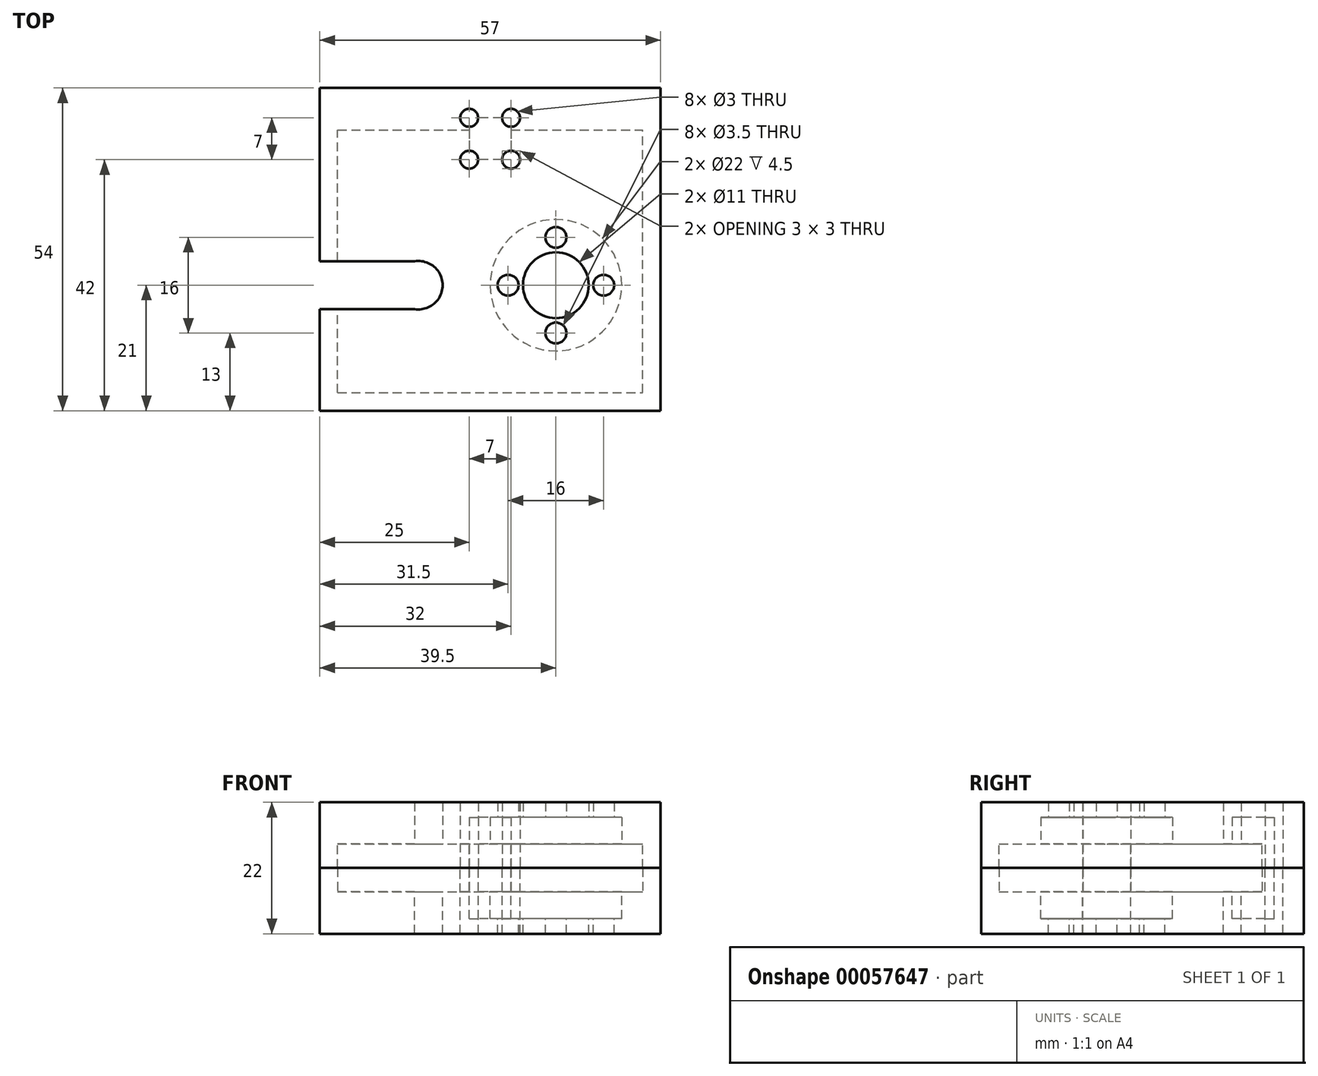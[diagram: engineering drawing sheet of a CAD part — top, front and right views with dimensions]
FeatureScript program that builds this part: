
annotation { "Feature Type Name" : "Feature", "Feature Type Description" : "" }
export const myFeature = defineFeature(function(context is Context, id is Id, definition is map)
    precondition{}
    {
        {
            var Q0;
            Q0=qCreatedBy(makeId("Top.planeOp"),FACE);
            var sketch = newSketch(context, id + "F0", { "sketchPlane" : qUnion([Q0])});
            skCircle(sketch, "E0", {"center": v(0, 0) * mm, "radius": 5.5 * mm});
            skCircle(sketch, "E1", {"center": v(0, 0) * mm, "radius": 8 * mm, "construction": true});
            skCircle(sketch, "E2", {"center": v(0, 8) * mm, "radius": 1.75 * mm});
            skCircle(sketch, "E3", {"center": v(8, 0) * mm, "radius": 1.75 * mm});
            skCircle(sketch, "E4", {"center": v(0, -8) * mm, "radius": 1.75 * mm});
            skCircle(sketch, "E5", {"center": v(-8, 0) * mm, "radius": 1.75 * mm});
            skCircle(sketch, "E6", {"center": v(0, 0) * mm, "radius": 11 * mm});
            skLineSegment(sketch, "E7.rect.bottom", {"start": v(-7.5, 28) * mm, "end": v(-14.5, 28) * mm});
            skLineSegment(sketch, "E7.rect.top", {"start": v(-7.5, 21) * mm, "end": v(-14.5, 21) * mm});
            skLineSegment(sketch, "E7.rect.left", {"start": v(-7.5, 28) * mm, "end": v(-7.5, 21) * mm});
            skLineSegment(sketch, "E7.rect.right", {"start": v(-14.5, 28) * mm, "end": v(-14.5, 21) * mm});
            skLineSegment(sketch, "E8.rect.bottom", {"start": v(14.5, -21) * mm, "end": v(-36.5, -21) * mm});
            skLineSegment(sketch, "E8.rect.top", {"start": v(14.5, 33) * mm, "end": v(-36.5, 33) * mm});
            skLineSegment(sketch, "E8.rect.left", {"start": v(14.5, -21) * mm, "end": v(14.5, 33) * mm});
            skLineSegment(sketch, "E8.rect.right", {"start": v(-36.5, -21) * mm, "end": v(-36.5, 33) * mm});
            skPoint(sketch, "E8.rect.middle", {"position": v(-11, 6) * mm});
            skLineSegment(sketch, "E9", {"start": v(-36.5, 26) * mm, "end": v(-14.5, 26) * mm});
            skLineSegment(sketch, "E10", {"start": v(-36.5, -18) * mm, "end": v(14.5, -18) * mm});
            skCircle(sketch, "E11", {"center": v(-14.5, 28) * mm, "radius": 1.5 * mm});
            skCircle(sketch, "E12", {"center": v(-7.5, 28) * mm, "radius": 1.5 * mm});
            skCircle(sketch, "E13", {"center": v(-7.5, 21) * mm, "radius": 1.5 * mm});
            skCircle(sketch, "E14", {"center": v(-14.5, 21) * mm, "radius": 1.5 * mm});
            skCircle(sketch, "E15", {"center": v(-23, 0) * mm, "radius": 4.05 * mm});
            skLineSegment(sketch, "E16.bottom", {"start": v(-39.5, 33) * mm, "end": v(17.5, 33) * mm});
            skLineSegment(sketch, "E16.top", {"start": v(-39.5, -21) * mm, "end": v(17.5, -21) * mm});
            skLineSegment(sketch, "E16.left", {"start": v(-39.5, 33) * mm, "end": v(-39.5, -21) * mm});
            skLineSegment(sketch, "E16.right", {"start": v(17.5, 33) * mm, "end": v(17.5, -21) * mm});
            skPoint(sketch, "E17.endSnap0", {"position": v(-11, 21) * mm});
            skLineSegment(sketch, "E18", {"start": v(-11, 21) * mm, "end": v(-11, 28) * mm, "construction": true});
            skLineSegment(sketch, "E19", {"start": v(-11, 26) * mm, "end": v(-11, 33) * mm, "construction": true});
            skLineSegment(sketch, "E20", {"start": v(-11, 26) * mm, "end": v(-11, 24.5) * mm, "construction": true});
            skLineSegment(sketch, "E21.trimOffspring", {"start": v(-7.5, 26) * mm, "end": v(14.5, 26) * mm});
            skLineSegment(sketch, "E22", {"start": v(-23, 0) * mm, "end": v(-39.5, 0) * mm, "construction": true});
            skLineSegment(sketch, "E23.0", {"start": v(-23, 4) * mm, "end": v(-39.5, 4) * mm});
            skLineSegment(sketch, "E24.0", {"start": v(-23, -4) * mm, "end": v(-39.5, -4) * mm});
            skSolve(sketch);
        }
        {
            var Q0;
            Q0=makeQuery(id+"F0.imprint","IMPRINT",FACE,{"disambiguationData":[TD([[makeQuery(id+"F0.imprint","IMPRINT",EDGE,{"derivedFrom":sQuery(id+"F0.wireOp",EDGE,"E6")}),-1.0]])]});
            var Q1;
            {var subQ0=sQuery(id+"F0.wireOp",EDGE,"E9");Q1=makeQuery(id+"F0.imprint","IMPRINT",FACE,{"disambiguationData":[TD([[makeQuery(id+"F0.imprint","IMPRINT",EDGE,{"derivedFrom":subQ0}),1.0]])]});}
            var Q2;
            {var subQ3=sQuery(id+"F0.wireOp",EDGE,"E10");Q2=makeQuery(id+"F0.imprint","IMPRINT",FACE,{"disambiguationData":[TD([[makeQuery(id+"F0.imprint","IMPRINT",EDGE,{"derivedFrom":subQ3}),-1.0]])]});}
            var Q3;
            {var subQ3=sQuery(id+"F0.wireOp",EDGE,"E16.right");Q3=makeQuery(id+"F0.imprint","IMPRINT",FACE,{"disambiguationData":[TD([[makeQuery(id+"F0.imprint","IMPRINT",EDGE,{"derivedFrom":subQ3}),-1.0]])]});}
            var Q4;
            {var subQ5=sQuery(id+"F0.wireOp",EDGE,"E8.rect.right");var subQ8=makeQuery(id+"F0.imprint","INTERSECT",VERTEX,{"derivedFrom":[subQ5,sQuery(id+"F0.wireOp",EDGE,"E9")]});Q4=makeQuery(id+"F0.imprint","IMPRINT",FACE,{"disambiguationData":[TD([[makeQuery(id+"F0.imprint","IMPRINT",EDGE,{"disambiguationData":[TD([[subQ8,1.0]])],"derivedFrom":subQ5}),1.0]])]});}
            var Q5;
            {var subQ0=sQuery(id+"F0.wireOp",EDGE,"E16.top");var subQ1=sQuery(id+"F0.wireOp",EDGE,"E8.rect.right");var subQ2=makeQuery(id+"F0.imprint","INTERSECT",VERTEX,{"derivedFrom":[subQ1,subQ0]});Q5=makeQuery(id+"F0.imprint","IMPRINT",FACE,{"disambiguationData":[TD([[makeQuery(id+"F0.imprint","IMPRINT",EDGE,{"disambiguationData":[TD([[subQ2,-1.0]])],"derivedFrom":subQ1}),1.0]])]});}
            extrude(context, id + "F1", {"entities" : qUnion([Q0, Q1, Q2, Q3, Q4, Q5]), "depth" : 4.5 * mm});
        }
        {
            var Q0;
            {var subQ3=sQuery(id+"F0.wireOp",EDGE,"E16.right");Q0=makeQuery(id+"F0.imprint","IMPRINT",FACE,{"disambiguationData":[TD([[makeQuery(id+"F0.imprint","IMPRINT",EDGE,{"derivedFrom":subQ3}),-1.0]])]});}
            var Q1;
            {var subQ0=sQuery(id+"F0.wireOp",EDGE,"E9");Q1=makeQuery(id+"F0.imprint","IMPRINT",FACE,{"disambiguationData":[TD([[makeQuery(id+"F0.imprint","IMPRINT",EDGE,{"derivedFrom":subQ0}),1.0]])]});}
            var Q2;
            {var subQ3=sQuery(id+"F0.wireOp",EDGE,"E10");Q2=makeQuery(id+"F0.imprint","IMPRINT",FACE,{"disambiguationData":[TD([[makeQuery(id+"F0.imprint","IMPRINT",EDGE,{"derivedFrom":subQ3}),-1.0]])]});}
            var Q3;
            {var subQ5=sQuery(id+"F0.wireOp",EDGE,"E8.rect.right");var subQ8=makeQuery(id+"F0.imprint","INTERSECT",VERTEX,{"derivedFrom":[subQ5,sQuery(id+"F0.wireOp",EDGE,"E9")]});Q3=makeQuery(id+"F0.imprint","IMPRINT",FACE,{"disambiguationData":[TD([[makeQuery(id+"F0.imprint","IMPRINT",EDGE,{"disambiguationData":[TD([[subQ8,1.0]])],"derivedFrom":subQ5}),1.0]])]});}
            var Q4;
            {var subQ0=sQuery(id+"F0.wireOp",EDGE,"E16.top");var subQ1=sQuery(id+"F0.wireOp",EDGE,"E8.rect.right");var subQ2=makeQuery(id+"F0.imprint","INTERSECT",VERTEX,{"derivedFrom":[subQ1,subQ0]});Q4=makeQuery(id+"F0.imprint","IMPRINT",FACE,{"disambiguationData":[TD([[makeQuery(id+"F0.imprint","IMPRINT",EDGE,{"disambiguationData":[TD([[subQ2,-1.0]])],"derivedFrom":subQ1}),1.0]])]});}
            extrude(context, id + "F2", {"entities" : qUnion([Q0, Q1, Q2, Q3, Q4]), "operationType" : NewBodyOperationType.ADD, "oppositeDirection" : true, "depth" : 4 * mm});
        }
        {
            var Q0;
            Q0=makeQuery(id+"F1.opExtrude","CAP_FACE",FACE,{"disambiguationData":[OSD([sQuery(id+"F0.wireOp",EDGE,"E6"),sQuery(id+"F0.wireOp",EDGE,"E7.rect.bottom"),sQuery(id+"F0.wireOp",EDGE,"E7.rect.top"),sQuery(id+"F0.wireOp",EDGE,"E7.rect.left"),sQuery(id+"F0.wireOp",EDGE,"E7.rect.right"),sQuery(id+"F0.wireOp",EDGE,"E11"),sQuery(id+"F0.wireOp",EDGE,"E12"),sQuery(id+"F0.wireOp",EDGE,"E13"),sQuery(id+"F0.wireOp",EDGE,"E14"),sQuery(id+"F0.wireOp",EDGE,"E15"),sQuery(id+"F0.wireOp",EDGE,"E16.bottom"),sQuery(id+"F0.wireOp",EDGE,"E16.top"),sQuery(id+"F0.wireOp",EDGE,"E16.left"),sQuery(id+"F0.wireOp",EDGE,"E16.right"),sQuery(id+"F0.wireOp",EDGE,"E23.0"),sQuery(id+"F0.wireOp",EDGE,"E24.0")])],"isStart":false});
            var sketch = newSketch(context, id + "F3", { "sketchPlane" : qUnion([Q0])});
            skLineSegment(sketch, "E25.0", {"start": v(-39.5, -21) * mm, "end": v(17.5, -21) * mm});
            skLineSegment(sketch, "E26.0", {"start": v(17.5, 33) * mm, "end": v(17.5, -21) * mm});
            skLineSegment(sketch, "E27.0", {"start": v(-39.5, 33) * mm, "end": v(17.5, 33) * mm});
            skLineSegment(sketch, "E28.0.1", {"start": v(-39.5, -4) * mm, "end": v(-39.5, -21) * mm});
            skLineSegment(sketch, "E28.0.3", {"start": v(-39.5, -21) * mm, "end": v(-39.5, -4) * mm});
            skLineSegment(sketch, "E29.0", {"start": v(-39.5, 33) * mm, "end": v(-39.5, 4) * mm});
            skLineSegment(sketch, "E30.0", {"start": v(-23.63, 4) * mm, "end": v(-39.5, 4) * mm});
            skLineSegment(sketch, "E31.0", {"start": v(-23.63, -4) * mm, "end": v(-39.5, -4) * mm});
            skArc(sketch, "E32.0.0", {"start": v(-23.63, 4) * mm, "mid": v(-18.95, 0) * mm, "end": v(-23.63, -4) * mm});
            skArc(sketch, "E32.0.2", {"start": v(-23.63, -4) * mm, "mid": v(-18.95, 0) * mm, "end": v(-23.63, 4) * mm});
            skCircle(sketch, "E33.0", {"center": v(0, 0) * mm, "radius": 5.5 * mm});
            skCircle(sketch, "E34.0", {"center": v(0, 8) * mm, "radius": 1.75 * mm});
            skCircle(sketch, "E35.0", {"center": v(8, 0) * mm, "radius": 1.75 * mm});
            skCircle(sketch, "E36.0", {"center": v(0, -8) * mm, "radius": 1.75 * mm});
            skCircle(sketch, "E37.0", {"center": v(-8, 0) * mm, "radius": 1.75 * mm});
            skCircle(sketch, "E38.0", {"center": v(-14.5, 21) * mm, "radius": 1.5 * mm});
            skCircle(sketch, "E39.0", {"center": v(-7.5, 21) * mm, "radius": 1.5 * mm});
            skCircle(sketch, "E40.0", {"center": v(-14.5, 28) * mm, "radius": 1.5 * mm});
            skCircle(sketch, "E41.0", {"center": v(-7.5, 28) * mm, "radius": 1.5 * mm});
            skSolve(sketch);
        }
        {
            var Q0;
            Q0 = qSketchRegion(id + "F3", true);
            extrude(context, id + "F4", {"entities" : qUnion([Q0]), "operationType" : NewBodyOperationType.ADD, "depth" : 2.5 * mm});
        }
        {
            var Q0;
            Q0=makeQuery(id+"F1.opExtrude","SWEPT_BODY",BODY,{"disambiguationData":[OSD([sQuery(id+"F0.wireOp",EDGE,"E6"),sQuery(id+"F0.wireOp",EDGE,"E7.rect.bottom"),sQuery(id+"F0.wireOp",EDGE,"E7.rect.top"),sQuery(id+"F0.wireOp",EDGE,"E7.rect.left"),sQuery(id+"F0.wireOp",EDGE,"E7.rect.right"),sQuery(id+"F0.wireOp",EDGE,"E11"),sQuery(id+"F0.wireOp",EDGE,"E12"),sQuery(id+"F0.wireOp",EDGE,"E13"),sQuery(id+"F0.wireOp",EDGE,"E14"),sQuery(id+"F0.wireOp",EDGE,"E15"),sQuery(id+"F0.wireOp",EDGE,"E16.bottom"),sQuery(id+"F0.wireOp",EDGE,"E16.top"),sQuery(id+"F0.wireOp",EDGE,"E16.left"),sQuery(id+"F0.wireOp",EDGE,"E16.right")])]});
            var Q1;
            Q1=makeQuery(id+"F2.opExtrude","CAP_FACE",FACE,{"disambiguationData":[OSD([sQuery(id+"F0.wireOp",EDGE,"E7.rect.bottom"),sQuery(id+"F0.wireOp",EDGE,"E7.rect.left"),sQuery(id+"F0.wireOp",EDGE,"E7.rect.right"),sQuery(id+"F0.wireOp",EDGE,"E8.rect.left"),sQuery(id+"F0.wireOp",EDGE,"E8.rect.right"),sQuery(id+"F0.wireOp",EDGE,"E9"),sQuery(id+"F0.wireOp",EDGE,"E10"),sQuery(id+"F0.wireOp",EDGE,"E11"),sQuery(id+"F0.wireOp",EDGE,"E12"),sQuery(id+"F0.wireOp",EDGE,"E16.bottom"),sQuery(id+"F0.wireOp",EDGE,"E16.top"),sQuery(id+"F0.wireOp",EDGE,"E16.left"),sQuery(id+"F0.wireOp",EDGE,"E16.right"),sQuery(id+"F0.wireOp",EDGE,"E21.trimOffspring")])],"isStart":false});
            mirror(context, id + "F5", {"entities" : qUnion([Q0]), "mirrorPlane" : qUnion([Q1])});
        }
    });
